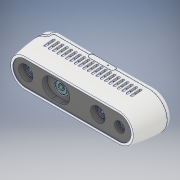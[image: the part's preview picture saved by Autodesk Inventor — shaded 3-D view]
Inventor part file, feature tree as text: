
AUTODESK INVENTOR PART (.ipt)
format: ipt  version: 2019 (Build 230136000, 136)  size: 1,141,248 bytes
history: imported  units: mm
features: other x8, projected_geometry x3, sketch x1, imported_body x1
ambient origin geometry x8: Origin, YZ Plane, XZ Plane, XY Plane, X Axis, Y Axis, Z Axis, Center Point
bodies: Solid1 (imported_parasolid), Solid2 (imported_parasolid), Solid3 (imported_parasolid), Solid4 (imported_parasolid), Solid5 (imported_parasolid), Solid6 (imported_parasolid), Solid7 (imported_parasolid), Solid8 (imported_parasolid)
feature tree (13):
  sketch  "Sketch1"
  projected_geometry  "Projected Loop1"
  projected_geometry  "Projected Loop2"
  projected_geometry  "Projected Loop3"
  other  "Cut-Extrude-Thin2[2]"
  other  "LPattern6[1]"
  other  "LPattern6[2]"
  other  "LPattern6[3]"
  other  "LPattern6[4]"
  other  "LPattern6[5]"
  other  "Dome2"
  other  "Boss-Extrude6"
  imported_body  NMx_Import_Brep_tag  [imported B-rep: ~17 faces, bbox_mm=None]
